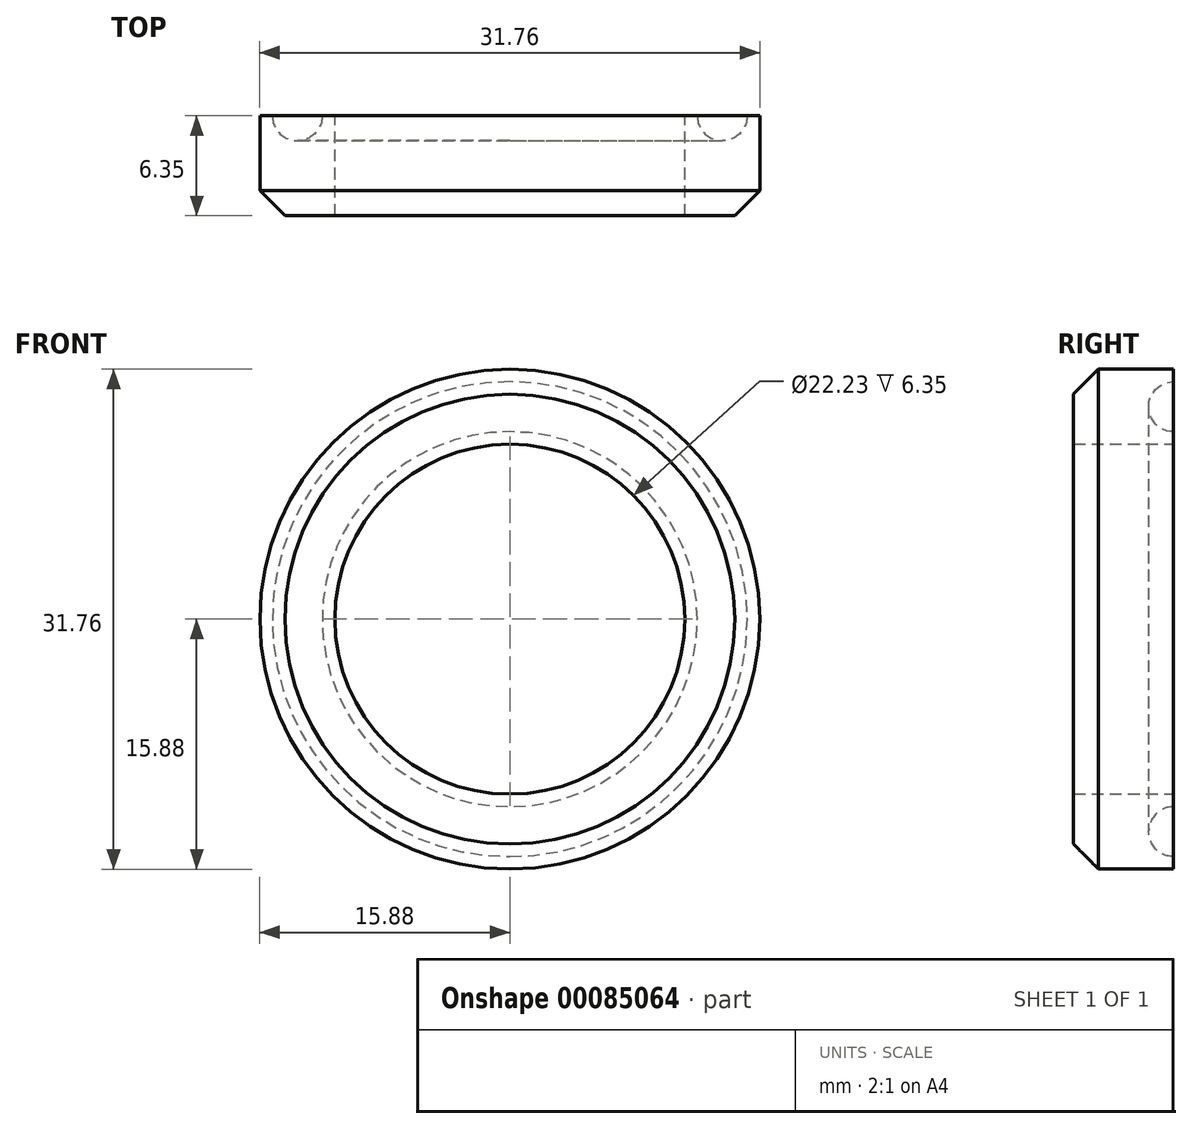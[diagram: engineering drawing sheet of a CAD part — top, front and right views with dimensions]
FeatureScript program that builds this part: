
annotation { "Feature Type Name" : "Feature", "Feature Type Description" : "" }
export const myFeature = defineFeature(function(context is Context, id is Id, definition is map)
    precondition{}
    {
        {
            var Q0;
            Q0=qCreatedBy(makeId("Front.planeOp"),FACE);
            var sketch = newSketch(context, id + "F0", { "sketchPlane" : qUnion([Q0])});
            skCircle(sketch, "E0", {"center": v(0, 0) * mm, "radius": 11.11 * mm});
            skCircle(sketch, "E1", {"center": v(0, 0) * mm, "radius": 15.88 * mm});
            skSolve(sketch);
        }
        {
            var Q0;
            Q0=makeQuery(id+"F0.imprint","IMPRINT",FACE,{"disambiguationData":[TD([[makeQuery(id+"F0.imprint","IMPRINT",EDGE,{"derivedFrom":sQuery(id+"F0.wireOp",EDGE,"E0")}),-1.0]])]});
            extrude(context, id + "F1", {"entities" : qUnion([Q0]), "depth" : 6.35 * mm});
        }
        {
            var Q0;
            Q0=makeQuery(id+"F1.opExtrude","CAP_EDGE",EDGE,{"disambiguationData":[OSD([sQuery(id+"F0.wireOp",EDGE,"E1")])],"isStart":false});
            chamfer(context, id + "F2", {"entities" : qUnion([Q0]), "width" : 1.59 * mm, "tangentPropagation" : true});
        }
        {
            var Q0;
            Q0=makeQuery(id+"F1.opExtrude","CAP_FACE",FACE,{"disambiguationData":[OSD([sQuery(id+"F0.wireOp",EDGE,"E0"),sQuery(id+"F0.wireOp",EDGE,"E1")])],"isStart":true});
            var sketch = newSketch(context, id + "F3", { "sketchPlane" : qUnion([Q0])});
            skPoint(sketch, "E2.0", {"position": v(0, 0) * mm});
            skCircle(sketch, "E2.1", {"center": v(0, 0) * mm, "radius": 11.11 * mm});
            skCircle(sketch, "E2.2", {"center": v(0, 0) * mm, "radius": 15.88 * mm});
            skCircle(sketch, "E3", {"center": v(0, 0) * mm, "radius": 11.9 * mm});
            skCircle(sketch, "E4", {"center": v(0, 0) * mm, "radius": 15.08 * mm});
            skSolve(sketch);
        }
        {
            var Q0;
            Q0=qCreatedBy(makeId("Right.planeOp"),FACE);
            var sketch = newSketch(context, id + "F4", { "sketchPlane" : qUnion([Q0])});
            skLineSegment(sketch, "E5.0", {"start": v(0, 15.08) * mm, "end": v(0, -15.08) * mm});
            skLineSegment(sketch, "E5.1", {"start": v(0, 11.9) * mm, "end": v(0, -11.9) * mm});
            skCircle(sketch, "E6", {"center": v(0, 13.5) * mm, "radius": 1.59 * mm});
            skSolve(sketch);
        }
        {
            var Q0;
            Q0 = qSketchRegion(id + "F4", true);
            var Q1;
            Q1=sQuery(id+"F3.wireOp",EDGE,"E3");
            sweep(context, id + "F5", {"operationType" : NewBodyOperationType.REMOVE, "profiles" : qUnion([Q0]), "path" : qUnion([Q1])});
        }
    });
